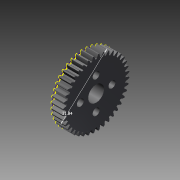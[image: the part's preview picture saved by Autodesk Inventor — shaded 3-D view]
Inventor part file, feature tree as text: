
AUTODESK INVENTOR PART (.ipt)
format: ipt  version: 2015 (Build 190159000, 159)  size: 453,120 bytes
history: native  units: in
note: dims shown in document units (in); Inventor stores cm internally (conversion verified against a paired STEP export)
features: other x6, sketch x1, imported_body x1, projected_geometry x1
ambient origin geometry x8: Origin, YZ Plane, XZ Plane, XY Plane, X Axis, Y Axis, Z Axis, Center Point
bodies: Body1 (feature_tree)
feature tree (9):
  other  "tetrix_739028_2012"
  other  "tetrix_739028_20121"
  other  "CENTER"
  other  "FRONT"
  other  "TOP"
  other  "RIGHT"
  sketch  "Sketch1"  dims[d0=1.2795in]
  imported_body  "Base1"
  projected_geometry  "Projected Loop1"
